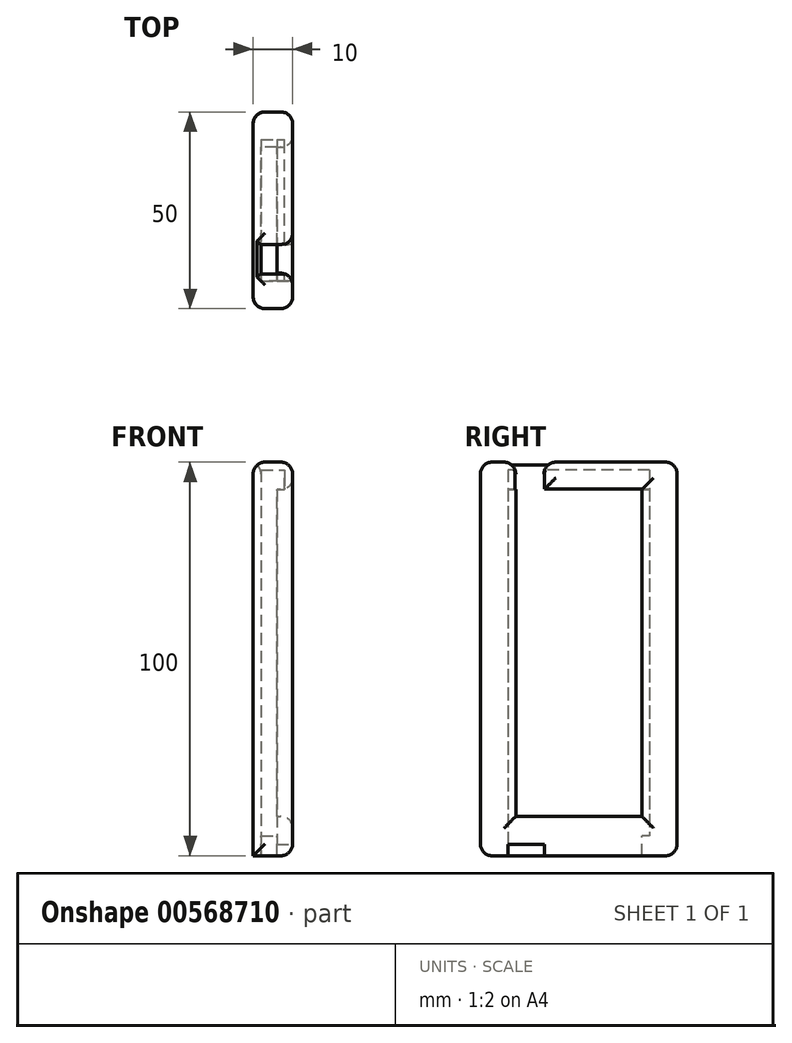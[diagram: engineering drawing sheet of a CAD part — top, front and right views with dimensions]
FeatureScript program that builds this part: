
annotation { "Feature Type Name" : "Feature", "Feature Type Description" : "" }
export const myFeature = defineFeature(function(context is Context, id is Id, definition is map)
    precondition{}
    {
        {
            var Q0;
            Q0=qCreatedBy(makeId("Right.planeOp"),FACE);
            var sketch = newSketch(context, id + "F0", { "sketchPlane" : qUnion([Q0])});
            skLineSegment(sketch, "E0.bottom", {"start": v(-37.24, 4.28) * mm, "end": v(12.76, 4.28) * mm});
            skLineSegment(sketch, "E0.top", {"start": v(-37.24, -95.72) * mm, "end": v(12.76, -95.72) * mm});
            skLineSegment(sketch, "E0.left", {"start": v(-37.24, 4.28) * mm, "end": v(-37.24, -95.72) * mm});
            skLineSegment(sketch, "E0.right", {"start": v(12.76, 4.28) * mm, "end": v(12.76, -95.72) * mm});
            skPoint(sketch, "E0.middle", {"position": v(-12.24, -45.72) * mm});
            skSolve(sketch);
        }
        {
            var Q0;
            Q0 = qSketchRegion(id + "F0", true);
            extrude(context, id + "F1", {"entities" : qUnion([Q0]), "depth" : 10 * mm, "offsetDistance" : 25 * mm});
        }
        {
            var Q0;
            Q0=makeQuery(id+"F1.opExtrude","CAP_FACE",FACE,{"disambiguationData":[OSD([sQuery(id+"F0.wireOp",EDGE,"E0.bottom"),sQuery(id+"F0.wireOp",EDGE,"E0.top"),sQuery(id+"F0.wireOp",EDGE,"E0.left"),sQuery(id+"F0.wireOp",EDGE,"E0.right")])],"isStart":false});
            var sketch = newSketch(context, id + "F2", { "sketchPlane" : qUnion([Q0])});
            skLineSegment(sketch, "E1.bottom", {"start": v(5.76, -2.72) * mm, "end": v(-30.24, -2.72) * mm});
            skLineSegment(sketch, "E1.top", {"start": v(5.76, -85.72) * mm, "end": v(-30.24, -85.72) * mm});
            skLineSegment(sketch, "E1.left", {"start": v(5.76, -2.72) * mm, "end": v(5.76, -85.72) * mm});
            skLineSegment(sketch, "E1.right", {"start": v(-30.24, -2.72) * mm, "end": v(-30.24, -85.72) * mm});
            skSolve(sketch);
        }
        {
            var Q0;
            Q0 = qSketchRegion(id + "F2", true);
            extrude(context, id + "F3", {"entities" : qUnion([Q0]), "operationType" : NewBodyOperationType.REMOVE, "oppositeDirection" : true, "depth" : 8 * mm, "offsetDistance" : 25 * mm});
        }
        {
            var Q0;
            Q0=makeQuery(id+"F1.opExtrude","CAP_FACE",FACE,{"disambiguationData":[OSD([sQuery(id+"F0.wireOp",EDGE,"E0.bottom"),sQuery(id+"F0.wireOp",EDGE,"E0.top"),sQuery(id+"F0.wireOp",EDGE,"E0.left"),sQuery(id+"F0.wireOp",EDGE,"E0.right")])],"isStart":false});
            var sketch = newSketch(context, id + "F4", { "sketchPlane" : qUnion([Q0])});
            skLineSegment(sketch, "E2.bottom", {"start": v(-30.24, -85.72) * mm, "end": v(-28.24, -85.72) * mm});
            skLineSegment(sketch, "E2.top", {"start": v(-30.24, -2.72) * mm, "end": v(-28.24, -2.72) * mm});
            skLineSegment(sketch, "E2.left", {"start": v(-30.24, -85.72) * mm, "end": v(-30.24, -2.72) * mm});
            skLineSegment(sketch, "E2.right", {"start": v(-28.24, -85.72) * mm, "end": v(-28.24, -2.72) * mm});
            skSolve(sketch);
        }
        {
            var Q0;
            Q0 = qSketchRegion(id + "F4", true);
            extrude(context, id + "F5", {"entities" : qUnion([Q0]), "operationType" : NewBodyOperationType.ADD, "oppositeDirection" : true, "depth" : 4 * mm, "offsetDistance" : 25 * mm});
        }
        {
            var Q0;
            Q0=makeQuery(id+"F5.boolean.opBoolean","MERGE",FACE,{"derivedFrom":[makeQuery(id+"F1.opExtrude","CAP_FACE",FACE,{"disambiguationData":[OSD([sQuery(id+"F0.wireOp",EDGE,"E0.bottom"),sQuery(id+"F0.wireOp",EDGE,"E0.top"),sQuery(id+"F0.wireOp",EDGE,"E0.left"),sQuery(id+"F0.wireOp",EDGE,"E0.right")])],"isStart":false}),makeQuery(id+"F5.opExtrude","CAP_FACE",FACE,{"disambiguationData":[OSD([sQuery(id+"F4.wireOp",EDGE,"E2.bottom"),sQuery(id+"F4.wireOp",EDGE,"E2.top"),sQuery(id+"F4.wireOp",EDGE,"E2.left"),sQuery(id+"F4.wireOp",EDGE,"E2.right")])],"isStart":true})]});
            var sketch = newSketch(context, id + "F6", { "sketchPlane" : qUnion([Q0])});
            skLineSegment(sketch, "E3.bottom", {"start": v(5.76, -85.72) * mm, "end": v(3.76, -85.72) * mm});
            skLineSegment(sketch, "E3.top", {"start": v(5.76, -2.72) * mm, "end": v(3.76, -2.72) * mm});
            skLineSegment(sketch, "E3.left", {"start": v(5.76, -85.72) * mm, "end": v(5.76, -2.72) * mm});
            skLineSegment(sketch, "E3.right", {"start": v(3.76, -85.72) * mm, "end": v(3.76, -2.72) * mm});
            skSolve(sketch);
        }
        {
            var Q0;
            Q0 = qSketchRegion(id + "F6", true);
            extrude(context, id + "F7", {"entities" : qUnion([Q0]), "operationType" : NewBodyOperationType.ADD, "oppositeDirection" : true, "depth" : 4 * mm, "offsetDistance" : 25 * mm});
        }
        {
            var Q0;
            Q0=makeQuery(id+"F3.boolean.opBoolean","COPY",FACE,{"derivedFrom":makeQuery(id+"F3.opExtrude","SWEPT_FACE",FACE,{"disambiguationData":[OSD([sQuery(id+"F2.wireOp",EDGE,"E1.top")])]})});
            var sketch = newSketch(context, id + "F8", { "sketchPlane" : qUnion([Q0])});
            skLineSegment(sketch, "E4.bottom", {"start": v(2, -30.24) * mm, "end": v(6, -30.24) * mm});
            skLineSegment(sketch, "E4.top", {"start": v(2, 3.76) * mm, "end": v(6, 3.76) * mm});
            skLineSegment(sketch, "E4.left", {"start": v(2, -30.24) * mm, "end": v(2, 3.76) * mm});
            skLineSegment(sketch, "E4.right", {"start": v(6, -30.24) * mm, "end": v(6, 3.76) * mm});
            skSolve(sketch);
        }
        {
            var Q0;
            Q0 = qSketchRegion(id + "F8", true);
            var Q1;
            Q1=makeQuery(id+"F1.opExtrude","SWEPT_FACE",FACE,{"disambiguationData":[OSD([sQuery(id+"F0.wireOp",EDGE,"E0.top")])]});
            extrude(context, id + "F9", {"entities" : qUnion([Q0]), "operationType" : NewBodyOperationType.REMOVE, "endBound" : BoundingType.UP_TO_SURFACE, "oppositeDirection" : true, "depth" : 25 * mm, "endBoundEntityFace" : qUnion([Q1]), "offsetDistance" : 25 * mm});
        }
        {
            var Q0;
            Q0=makeQuery(id+"F3.boolean.opBoolean","COPY",FACE,{"derivedFrom":makeQuery(id+"F3.opExtrude","SWEPT_FACE",FACE,{"disambiguationData":[OSD([sQuery(id+"F2.wireOp",EDGE,"E1.bottom")])]})});
            var sketch = newSketch(context, id + "F10", { "sketchPlane" : qUnion([Q0])});
            skLineSegment(sketch, "E5.bottom", {"start": v(10, 28.24) * mm, "end": v(2, 28.24) * mm});
            skLineSegment(sketch, "E5.top", {"start": v(10, 21.09) * mm, "end": v(2, 21.09) * mm});
            skLineSegment(sketch, "E5.left", {"start": v(10, 28.24) * mm, "end": v(10, 21.09) * mm});
            skLineSegment(sketch, "E5.right", {"start": v(2, 28.24) * mm, "end": v(2, 21.09) * mm});
            skSolve(sketch);
        }
        {
            var Q0;
            Q0 = qSketchRegion(id + "F10", true);
            var Q1;
            Q1=makeQuery(id+"F1.opExtrude","SWEPT_FACE",FACE,{"disambiguationData":[OSD([sQuery(id+"F0.wireOp",EDGE,"E0.bottom")])]});
            extrude(context, id + "F11", {"entities" : qUnion([Q0]), "operationType" : NewBodyOperationType.REMOVE, "endBound" : BoundingType.UP_TO_SURFACE, "oppositeDirection" : true, "depth" : 25 * mm, "endBoundEntityFace" : qUnion([Q1]), "offsetDistance" : 25 * mm});
        }
        {
            var Q0;
            Q0=makeQuery(id+"F1.opExtrude","SWEPT_FACE",FACE,{"disambiguationData":[OSD([sQuery(id+"F0.wireOp",EDGE,"E0.bottom")])]});
            var Q1;
            Q1=makeQuery(id+"F1.opExtrude","SWEPT_FACE",FACE,{"disambiguationData":[OSD([sQuery(id+"F0.wireOp",EDGE,"E0.right")])]});
            fillet(context, id + "F12", {"entities" : qUnion([Q0, Q1]), "radius" : 3 * mm, "tangentPropagation" : true, "allowEdgeOverflow" : false});
        }
        {
            var Q0;
            Q0=makeQuery(id+"F7.boolean.opBoolean","MERGE",FACE,{"derivedFrom":[makeQuery(id+"F5.boolean.opBoolean","MERGE",FACE,{"derivedFrom":[makeQuery(id+"F1.opExtrude","CAP_FACE",FACE,{"disambiguationData":[OSD([sQuery(id+"F0.wireOp",EDGE,"E0.bottom"),sQuery(id+"F0.wireOp",EDGE,"E0.top"),sQuery(id+"F0.wireOp",EDGE,"E0.left"),sQuery(id+"F0.wireOp",EDGE,"E0.right")])],"isStart":false}),makeQuery(id+"F5.opExtrude","CAP_FACE",FACE,{"disambiguationData":[OSD([sQuery(id+"F4.wireOp",EDGE,"E2.bottom"),sQuery(id+"F4.wireOp",EDGE,"E2.top"),sQuery(id+"F4.wireOp",EDGE,"E2.left"),sQuery(id+"F4.wireOp",EDGE,"E2.right")])],"isStart":true})]}),makeQuery(id+"F7.opExtrude","CAP_FACE",FACE,{"disambiguationData":[OSD([sQuery(id+"F6.wireOp",EDGE,"E3.bottom"),sQuery(id+"F6.wireOp",EDGE,"E3.top"),sQuery(id+"F6.wireOp",EDGE,"E3.left"),sQuery(id+"F6.wireOp",EDGE,"E3.right")])],"isStart":true})]});
            var Q1;
            Q1=makeQuery(id+"F1.opExtrude","SWEPT_FACE",FACE,{"disambiguationData":[OSD([sQuery(id+"F0.wireOp",EDGE,"E0.left")])]});
            fillet(context, id + "F13", {"entities" : qUnion([Q0, Q1]), "radius" : 3 * mm, "tangentPropagation" : true, "allowEdgeOverflow" : false});
        }
        {
            var Q0;
            {var subQ1=sQuery(id+"F2.wireOp",EDGE,"E1.right");var subQ2=sQuery(id+"F2.wireOp",EDGE,"E1.bottom");Q0=makeQuery(id+"F11.boolean.opBoolean","SPLIT",FACE,{"disambiguationData":[TD([makeQuery(id+"F3.boolean.opBoolean","COPY",FACE,{"derivedFrom":makeQuery(id+"F3.opExtrude","SWEPT_FACE",FACE,{"disambiguationData":[OSD([subQ1])]})})])],"derivedFrom":makeQuery(id+"F3.boolean.opBoolean","COPY",FACE,{"derivedFrom":makeQuery(id+"F3.opExtrude","SWEPT_FACE",FACE,{"disambiguationData":[OSD([subQ2])]})})});}
            var sketch = newSketch(context, id + "F14", { "sketchPlane" : qUnion([Q0])});
            skLineSegment(sketch, "E6.bottom", {"start": v(2, 30.24) * mm, "end": v(8, 30.24) * mm});
            skLineSegment(sketch, "E6.top", {"start": v(2, -5.76) * mm, "end": v(8, -5.76) * mm});
            skLineSegment(sketch, "E6.left", {"start": v(2, 30.24) * mm, "end": v(2, -5.76) * mm});
            skLineSegment(sketch, "E6.right", {"start": v(8, 30.24) * mm, "end": v(8, -5.76) * mm});
            skSolve(sketch);
        }
        {
            var Q0;
            Q0 = qSketchRegion(id + "F14", true);
            extrude(context, id + "F15", {"entities" : qUnion([Q0]), "operationType" : NewBodyOperationType.REMOVE, "oppositeDirection" : true, "depth" : 5 * mm, "offsetDistance" : 25 * mm});
        }
        {
            var Q0;
            {var subQ0=sQuery(id+"F2.wireOp",EDGE,"E1.left");var subQ1=sQuery(id+"F2.wireOp",EDGE,"E1.top");var subQ2=makeQuery(id+"F3.boolean.opBoolean","COPY",FACE,{"derivedFrom":makeQuery(id+"F3.opExtrude","SWEPT_FACE",FACE,{"disambiguationData":[OSD([subQ1])]})});Q0=makeQuery(id+"F9.boolean.opBoolean","SPLIT",FACE,{"disambiguationData":[TD([makeQuery(id+"F3.boolean.opBoolean","COPY",FACE,{"derivedFrom":makeQuery(id+"F3.opExtrude","SWEPT_FACE",FACE,{"disambiguationData":[OSD([subQ0])]})})])],"derivedFrom":subQ2});}
            var sketch = newSketch(context, id + "F16", { "sketchPlane" : qUnion([Q0])});
            skLineSegment(sketch, "E7.bottom", {"start": v(2, 3.76) * mm, "end": v(6, 3.76) * mm});
            skLineSegment(sketch, "E7.top", {"start": v(2, 5.76) * mm, "end": v(6, 5.76) * mm});
            skLineSegment(sketch, "E7.left", {"start": v(2, 3.76) * mm, "end": v(2, 5.76) * mm});
            skLineSegment(sketch, "E7.right", {"start": v(6, 3.76) * mm, "end": v(6, 5.76) * mm});
            skSolve(sketch);
        }
        {
            var Q0;
            Q0 = qSketchRegion(id + "F16", true);
            extrude(context, id + "F17", {"entities" : qUnion([Q0]), "operationType" : NewBodyOperationType.REMOVE, "oppositeDirection" : true, "depth" : 5 * mm, "offsetDistance" : 25 * mm});
        }
        {
            var Q0;
            Q0=makeQuery(id+"F1.opExtrude","SWEPT_FACE",FACE,{"disambiguationData":[OSD([sQuery(id+"F0.wireOp",EDGE,"E0.top")])]});
            var sketch = newSketch(context, id + "F18", { "sketchPlane" : qUnion([Q0])});
            skLineSegment(sketch, "E8.bottom", {"start": v(2, 30.24) * mm, "end": v(10.24, 30.24) * mm});
            skLineSegment(sketch, "E8.top", {"start": v(2, 21) * mm, "end": v(10.24, 21) * mm});
            skLineSegment(sketch, "E8.left", {"start": v(2, 30.24) * mm, "end": v(2, 21) * mm});
            skLineSegment(sketch, "E8.right", {"start": v(10.24, 30.24) * mm, "end": v(10.24, 21) * mm});
            skSolve(sketch);
        }
        {
            var Q0;
            Q0 = qSketchRegion(id + "F18", true);
            extrude(context, id + "F19", {"entities" : qUnion([Q0]), "operationType" : NewBodyOperationType.REMOVE, "oppositeDirection" : true, "depth" : 2.9 * mm, "offsetDistance" : 25 * mm});
        }
    });
